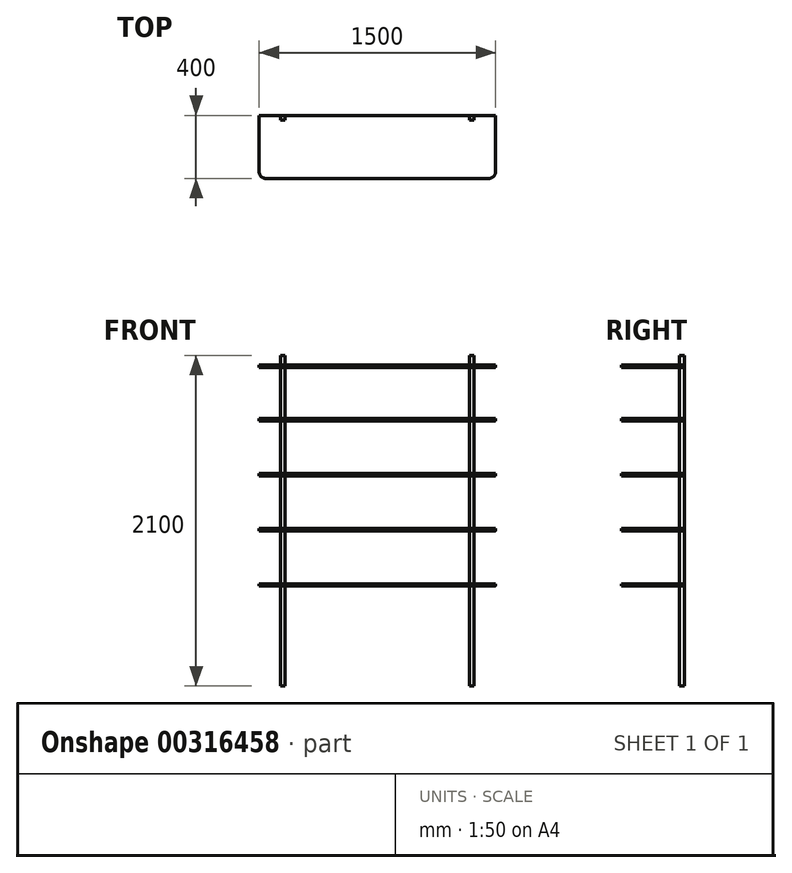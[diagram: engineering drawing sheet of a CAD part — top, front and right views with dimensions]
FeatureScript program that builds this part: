
annotation { "Feature Type Name" : "Feature", "Feature Type Description" : "" }
export const myFeature = defineFeature(function(context is Context, id is Id, definition is map)
    precondition{}
    {
        {
            assignVariable(context, id + "F0", {"name" : "Hauteur", "anyValue" : 2100});
        }
        {
            assignVariable(context, id + "F1", {"name" : "Ep", "anyValue" : 15});
        }
        {
            assignVariable(context, id + "F2", {"name" : "Niveau1", "anyValue" : 650});
        }
        {
            assignVariable(context, id + "F3", {"name" : "Niveau2", "anyValue" : 1000});
        }
        {
            assignVariable(context, id + "F4", {"name" : "Niveau3", "anyValue" : 1350});
        }
        {
            assignVariable(context, id + "F5", {"name" : "Niveau4", "anyValue" : 1700});
        }
        {
            assignVariable(context, id + "F6", {"name" : "Niveau5", "anyValue" : 2040});
        }
        {
            var Q0;
            Q0=qCreatedBy(makeId("Top.planeOp"),FACE);
            var sketch = newSketch(context, id + "F7", { "sketchPlane" : qUnion([Q0])});
            skLineSegment(sketch, "E0.bottom", {"start": v(-615, 0) * mm, "end": v(-585, 0) * mm});
            skLineSegment(sketch, "E0.top", {"start": v(-615, -30) * mm, "end": v(-585, -30) * mm});
            skLineSegment(sketch, "E0.left", {"start": v(-615, 0) * mm, "end": v(-615, -30) * mm});
            skLineSegment(sketch, "E0.right", {"start": v(-585, 0) * mm, "end": v(-585, -30) * mm});
            skLineSegment(sketch, "E1", {"start": v(0, 0) * mm, "end": v(0, -268.34) * mm, "construction": true});
            skLineSegment(sketch, "E2.MirrorCS", {"start": v(615, 0) * mm, "end": v(585, 0) * mm});
            skLineSegment(sketch, "E3.MirrorCS", {"start": v(615, -30) * mm, "end": v(585, -30) * mm});
            skLineSegment(sketch, "E4.MirrorCS", {"start": v(615, 0) * mm, "end": v(615, -30) * mm});
            skLineSegment(sketch, "E5.MirrorCS", {"start": v(585, 0) * mm, "end": v(585, -30) * mm});
            skSolve(sketch);
        }
        {
            var Q0;
            Q0=makeQuery(id+"F7.imprint","IMPRINT",FACE,{"disambiguationData":[TD([[makeQuery(id+"F7.imprint","IMPRINT",EDGE,{"derivedFrom":sQuery(id+"F7.wireOp",EDGE,"E0.bottom")}),-1.0]])]});
            var Q1;
            Q1=makeQuery(id+"F7.imprint","IMPRINT",FACE,{"disambiguationData":[TD([[makeQuery(id+"F7.imprint","IMPRINT",EDGE,{"derivedFrom":sQuery(id+"F7.wireOp",EDGE,"E2.MirrorCS")}),1.0]])]});
            extrude(context, id + "F8", {"entities" : qUnion([Q0, Q1]), "depth" : (getVariable(context, 'Hauteur')) * mm});
        }
        {
            var Q0;
            Q0=qCreatedBy(makeId("Top.planeOp"),FACE);
            cPlane(context, id + "F9", {"entities" : qUnion([Q0]), "cplaneType" : CPlaneType.OFFSET, "offset" : (getVariable(context, 'Niveau1')) * mm, "width" : 150 * mm, "height" : 150 * mm});
        }
        {
            var Q0;
            Q0=qCreatedBy(makeId("Top.planeOp"),FACE);
            cPlane(context, id + "F10", {"entities" : qUnion([Q0]), "cplaneType" : CPlaneType.OFFSET, "offset" : (getVariable(context, 'Niveau2')) * mm, "width" : 150 * mm, "height" : 150 * mm});
        }
        {
            var Q0;
            Q0=qCreatedBy(makeId("Top.planeOp"),FACE);
            cPlane(context, id + "F11", {"entities" : qUnion([Q0]), "cplaneType" : CPlaneType.OFFSET, "offset" : (getVariable(context, 'Niveau3')) * mm, "width" : 150 * mm, "height" : 150 * mm});
        }
        {
            var Q0;
            Q0=qCreatedBy(makeId("Top.planeOp"),FACE);
            cPlane(context, id + "F12", {"entities" : qUnion([Q0]), "cplaneType" : CPlaneType.OFFSET, "offset" : (getVariable(context, 'Niveau4')) * mm, "width" : 150 * mm, "height" : 150 * mm});
        }
        {
            var Q0;
            Q0=qCreatedBy(makeId("Top.planeOp"),FACE);
            cPlane(context, id + "F13", {"entities" : qUnion([Q0]), "cplaneType" : CPlaneType.OFFSET, "offset" : (getVariable(context, 'Niveau5')) * mm, "width" : 150 * mm, "height" : 150 * mm});
        }
        {
            var Q0;
            Q0=qCreatedBy(id+"F9.planeOp",FACE);
            var sketch = newSketch(context, id + "F14", { "sketchPlane" : qUnion([Q0])});
            skLineSegment(sketch, "E6", {"start": v(0, 0) * mm, "end": v(0, -284.12) * mm, "construction": true});
            skLineSegment(sketch, "E7", {"start": v(0, 0) * mm, "end": v(-585, 0) * mm});
            skLineSegment(sketch, "E8", {"start": v(-750, 0) * mm, "end": v(-750, -360) * mm});
            skLineSegment(sketch, "E9", {"start": v(-710, -400) * mm, "end": v(0, -400) * mm});
            skPoint(sketch, "E10.visualSharp", {"position": v(-750, -400) * mm});
            skArc(sketch, "E10.filletArc", {"start": v(-750, -360) * mm, "mid": v(-738.28, -388.28) * mm, "end": v(-710, -400) * mm});
            skLineSegment(sketch, "E11.0", {"start": v(-615, 0) * mm, "end": v(-615, -30) * mm});
            skLineSegment(sketch, "E12.0", {"start": v(-615, -30) * mm, "end": v(-585, -30) * mm});
            skLineSegment(sketch, "E13.0", {"start": v(-585, 0) * mm, "end": v(-585, -30) * mm});
            skLineSegment(sketch, "E14.trimOffspring", {"start": v(-615, 0) * mm, "end": v(-750, 0) * mm});
            skLineSegment(sketch, "E15.MirrorCS", {"start": v(0, 0) * mm, "end": v(585, 0) * mm});
            skLineSegment(sketch, "E16.MirrorCS", {"start": v(585, 0) * mm, "end": v(585, -30) * mm});
            skLineSegment(sketch, "E17.MirrorCS", {"start": v(615, -30) * mm, "end": v(585, -30) * mm});
            skLineSegment(sketch, "E18.MirrorCS", {"start": v(615, 0) * mm, "end": v(615, -30) * mm});
            skLineSegment(sketch, "E19.MirrorCS", {"start": v(615, 0) * mm, "end": v(750, 0) * mm});
            skLineSegment(sketch, "E20.MirrorCS", {"start": v(750, 0) * mm, "end": v(750, -360) * mm});
            skArc(sketch, "E21.MirrorCS", {"start": v(750, -360) * mm, "mid": v(738.28, -388.28) * mm, "end": v(710, -400) * mm});
            skLineSegment(sketch, "E22.MirrorCS", {"start": v(710, -400) * mm, "end": v(0, -400) * mm});
            skSolve(sketch);
        }
        {
            var Q0;
            Q0=makeQuery(id+"F14.imprint","IMPRINT",FACE,{"disambiguationData":[TD([[makeQuery(id+"F14.imprint","IMPRINT",EDGE,{"derivedFrom":sQuery(id+"F14.wireOp",EDGE,"E7")}),1.0]])]});
            extrude(context, id + "F15", {"entities" : qUnion([Q0]), "oppositeDirection" : true, "depth" : (getVariable(context, 'Ep')) * mm});
        }
        {
            var Q0;
            Q0=qCreatedBy(id+"F10.planeOp",FACE);
            var sketch = newSketch(context, id + "F16", { "sketchPlane" : qUnion([Q0])});
            skLineSegment(sketch, "E23.0", {"start": v(710, -400) * mm, "end": v(0, -400) * mm});
            skLineSegment(sketch, "E23.1", {"start": v(615, 0) * mm, "end": v(750, 0) * mm});
            skLineSegment(sketch, "E23.2", {"start": v(750, 0) * mm, "end": v(750, -360) * mm});
            skLineSegment(sketch, "E23.4", {"start": v(0, 0) * mm, "end": v(-585, 0) * mm});
            skLineSegment(sketch, "E23.5", {"start": v(-750, 0) * mm, "end": v(-750, -360) * mm});
            skLineSegment(sketch, "E23.6", {"start": v(-710, -400) * mm, "end": v(0, -400) * mm});
            skLineSegment(sketch, "E23.7", {"start": v(-615, 0) * mm, "end": v(-750, 0) * mm});
            skLineSegment(sketch, "E23.8", {"start": v(0, 0) * mm, "end": v(585, 0) * mm});
            skLineSegment(sketch, "E23.9", {"start": v(750, 0) * mm, "end": v(750, -360) * mm});
            skArc(sketch, "E24.0", {"start": v(-750, -360) * mm, "mid": v(-738.28, -388.28) * mm, "end": v(-710, -400) * mm});
            skArc(sketch, "E25.0", {"start": v(750, -360) * mm, "mid": v(738.28, -388.28) * mm, "end": v(710, -400) * mm});
            skLineSegment(sketch, "E26.0", {"start": v(-615, -30) * mm, "end": v(-585, -30) * mm});
            skLineSegment(sketch, "E27.0", {"start": v(-615, 0) * mm, "end": v(-615, -30) * mm});
            skLineSegment(sketch, "E28.0", {"start": v(-585, 0) * mm, "end": v(-585, -30) * mm});
            skLineSegment(sketch, "E29.0", {"start": v(585, 0) * mm, "end": v(585, -30) * mm});
            skLineSegment(sketch, "E30.0", {"start": v(615, -30) * mm, "end": v(585, -30) * mm});
            skPoint(sketch, "E31.0", {"position": v(615, -15) * mm});
            skLineSegment(sketch, "E32.0", {"start": v(615, 0) * mm, "end": v(615, -30) * mm});
            skSolve(sketch);
        }
        {
            var Q0;
            Q0=makeQuery(id+"F16.imprint","IMPRINT",FACE,{"disambiguationData":[TD([[makeQuery(id+"F16.imprint","IMPRINT",EDGE,{"derivedFrom":sQuery(id+"F16.wireOp",EDGE,"E23.0")}),-1.0]])]});
            extrude(context, id + "F17", {"entities" : qUnion([Q0]), "oppositeDirection" : true, "depth" : (getVariable(context, 'Ep')) * mm});
        }
        {
            var Q0;
            Q0=qCreatedBy(id+"F11.planeOp",FACE);
            var sketch = newSketch(context, id + "F18", { "sketchPlane" : qUnion([Q0])});
            skLineSegment(sketch, "E33.0", {"start": v(710, -400) * mm, "end": v(0, -400) * mm});
            skLineSegment(sketch, "E33.1", {"start": v(615, 0) * mm, "end": v(750, 0) * mm});
            skLineSegment(sketch, "E33.2", {"start": v(750, 0) * mm, "end": v(750, -360) * mm});
            skLineSegment(sketch, "E33.4", {"start": v(0, 0) * mm, "end": v(-585, 0) * mm});
            skLineSegment(sketch, "E33.5", {"start": v(-750, 0) * mm, "end": v(-750, -360) * mm});
            skLineSegment(sketch, "E33.6", {"start": v(-710, -400) * mm, "end": v(0, -400) * mm});
            skLineSegment(sketch, "E33.7", {"start": v(-615, 0) * mm, "end": v(-750, 0) * mm});
            skLineSegment(sketch, "E33.8", {"start": v(0, 0) * mm, "end": v(585, 0) * mm});
            skLineSegment(sketch, "E33.9", {"start": v(750, 0) * mm, "end": v(750, -360) * mm});
            skLineSegment(sketch, "E33.10", {"start": v(-710, -400) * mm, "end": v(710, -400) * mm});
            skArc(sketch, "E34.0", {"start": v(-750, -360) * mm, "mid": v(-738.28, -388.28) * mm, "end": v(-710, -400) * mm});
            skLineSegment(sketch, "E35.0", {"start": v(-615, 0) * mm, "end": v(-615, -30) * mm});
            skLineSegment(sketch, "E36.0", {"start": v(-615, -30) * mm, "end": v(-585, -30) * mm});
            skLineSegment(sketch, "E37.0", {"start": v(-585, 0) * mm, "end": v(-585, -30) * mm});
            skLineSegment(sketch, "E38.0", {"start": v(585, 0) * mm, "end": v(585, -30) * mm});
            skLineSegment(sketch, "E39.0", {"start": v(615, -30) * mm, "end": v(585, -30) * mm});
            skLineSegment(sketch, "E40.0", {"start": v(615, 0) * mm, "end": v(615, -30) * mm});
            skArc(sketch, "E41.0", {"start": v(750, -360) * mm, "mid": v(738.28, -388.28) * mm, "end": v(710, -400) * mm});
            skSolve(sketch);
        }
        {
            var Q0;
            Q0=makeQuery(id+"F18.imprint","IMPRINT",FACE,{"disambiguationData":[TD([[makeQuery(id+"F18.imprint","IMPRINT",EDGE,{"derivedFrom":sQuery(id+"F18.wireOp",EDGE,"E33.1")}),-1.0]])]});
            extrude(context, id + "F19", {"entities" : qUnion([Q0]), "oppositeDirection" : true, "depth" : (getVariable(context, 'Ep')) * mm});
        }
        {
            var Q0;
            Q0=qCreatedBy(id+"F12.planeOp",FACE);
            var sketch = newSketch(context, id + "F20", { "sketchPlane" : qUnion([Q0])});
            skPoint(sketch, "E42.0", {"position": v(710, -400) * mm});
            skLineSegment(sketch, "E43.0", {"start": v(710, -400) * mm, "end": v(0, -400) * mm});
            skLineSegment(sketch, "E43.1", {"start": v(615, 0) * mm, "end": v(750, 0) * mm});
            skLineSegment(sketch, "E43.2", {"start": v(750, 0) * mm, "end": v(750, -360) * mm});
            skArc(sketch, "E43.3", {"start": v(750, -360) * mm, "mid": v(738.28, -388.28) * mm, "end": v(710, -400) * mm});
            skLineSegment(sketch, "E43.5", {"start": v(0, 0) * mm, "end": v(-585, 0) * mm});
            skLineSegment(sketch, "E43.6", {"start": v(-750, 0) * mm, "end": v(-750, -360) * mm});
            skLineSegment(sketch, "E43.7", {"start": v(-710, -400) * mm, "end": v(0, -400) * mm});
            skLineSegment(sketch, "E43.8", {"start": v(-615, 0) * mm, "end": v(-750, 0) * mm});
            skLineSegment(sketch, "E43.9", {"start": v(0, 0) * mm, "end": v(585, 0) * mm});
            skLineSegment(sketch, "E43.10", {"start": v(750, 0) * mm, "end": v(750, -360) * mm});
            skLineSegment(sketch, "E43.11", {"start": v(-710, -400) * mm, "end": v(710, -400) * mm});
            skArc(sketch, "E43.12", {"start": v(750, -360) * mm, "mid": v(738.28, -388.28) * mm, "end": v(710, -400) * mm});
            skLineSegment(sketch, "E44.0", {"start": v(615, 0) * mm, "end": v(615, -30) * mm});
            skLineSegment(sketch, "E45.0", {"start": v(615, -30) * mm, "end": v(585, -30) * mm});
            skLineSegment(sketch, "E46.0", {"start": v(585, 0) * mm, "end": v(585, -30) * mm});
            skLineSegment(sketch, "E47.0", {"start": v(-615, 0) * mm, "end": v(-615, -30) * mm});
            skLineSegment(sketch, "E48.0", {"start": v(-615, -30) * mm, "end": v(-585, -30) * mm});
            skLineSegment(sketch, "E49.0", {"start": v(-585, 0) * mm, "end": v(-585, -30) * mm});
            skPoint(sketch, "E50.0", {"position": v(-738.28, -388.28) * mm});
            skArc(sketch, "E51.0", {"start": v(-750, -360) * mm, "mid": v(-738.28, -388.28) * mm, "end": v(-710, -400) * mm});
            skSolve(sketch);
        }
        {
            var Q0;
            Q0=makeQuery(id+"F20.imprint","IMPRINT",FACE,{"disambiguationData":[TD([[makeQuery(id+"F20.imprint","IMPRINT",EDGE,{"derivedFrom":sQuery(id+"F20.wireOp",EDGE,"E43.1")}),-1.0]])]});
            extrude(context, id + "F21", {"entities" : qUnion([Q0]), "oppositeDirection" : true, "depth" : (getVariable(context, 'Ep')) * mm});
        }
        {
            var Q0;
            Q0=qCreatedBy(id+"F13.planeOp",FACE);
            var sketch = newSketch(context, id + "F22", { "sketchPlane" : qUnion([Q0])});
            skLineSegment(sketch, "E52.0", {"start": v(710, -400) * mm, "end": v(0, -400) * mm});
            skLineSegment(sketch, "E52.1", {"start": v(615, 0) * mm, "end": v(750, 0) * mm});
            skLineSegment(sketch, "E52.2", {"start": v(750, 0) * mm, "end": v(750, -360) * mm});
            skLineSegment(sketch, "E52.4", {"start": v(0, 0) * mm, "end": v(-585, 0) * mm});
            skLineSegment(sketch, "E52.5", {"start": v(-750, 0) * mm, "end": v(-750, -360) * mm});
            skLineSegment(sketch, "E52.6", {"start": v(-710, -400) * mm, "end": v(0, -400) * mm});
            skLineSegment(sketch, "E52.7", {"start": v(-615, 0) * mm, "end": v(-750, 0) * mm});
            skLineSegment(sketch, "E52.8", {"start": v(0, 0) * mm, "end": v(585, 0) * mm});
            skLineSegment(sketch, "E52.9", {"start": v(-710, -400) * mm, "end": v(710, -400) * mm});
            skLineSegment(sketch, "E52.10", {"start": v(-710, -400) * mm, "end": v(710, -400) * mm});
            skLineSegment(sketch, "E52.11", {"start": v(750, 0) * mm, "end": v(750, -360) * mm});
            skLineSegment(sketch, "E52.12", {"start": v(-750, 0) * mm, "end": v(-750, -360) * mm});
            skLineSegment(sketch, "E52.13", {"start": v(750, 0) * mm, "end": v(750, -360) * mm});
            skLineSegment(sketch, "E52.14", {"start": v(-585, 0) * mm, "end": v(585, 0) * mm});
            skLineSegment(sketch, "E52.15", {"start": v(750, 0) * mm, "end": v(750, -360) * mm});
            skLineSegment(sketch, "E52.16", {"start": v(-710, -400) * mm, "end": v(710, -400) * mm});
            skArc(sketch, "E53.0", {"start": v(750, -360) * mm, "mid": v(738.28, -388.28) * mm, "end": v(710, -400) * mm});
            skLineSegment(sketch, "E54.0", {"start": v(615, 0) * mm, "end": v(615, -30) * mm});
            skLineSegment(sketch, "E55.0", {"start": v(615, -30) * mm, "end": v(585, -30) * mm});
            skLineSegment(sketch, "E56.0", {"start": v(585, 0) * mm, "end": v(585, -30) * mm});
            skLineSegment(sketch, "E57.0", {"start": v(-585, 0) * mm, "end": v(-585, -30) * mm});
            skLineSegment(sketch, "E58.0", {"start": v(-615, -30) * mm, "end": v(-585, -30) * mm});
            skLineSegment(sketch, "E59.0", {"start": v(-615, 0) * mm, "end": v(-615, -30) * mm});
            skArc(sketch, "E60.0", {"start": v(-750, -360) * mm, "mid": v(-738.28, -388.28) * mm, "end": v(-710, -400) * mm});
            skSolve(sketch);
        }
        {
            var Q0;
            Q0=makeQuery(id+"F22.imprint","IMPRINT",FACE,{"disambiguationData":[TD([[makeQuery(id+"F22.imprint","IMPRINT",EDGE,{"derivedFrom":sQuery(id+"F22.wireOp",EDGE,"E52.1")}),-1.0]])]});
            extrude(context, id + "F23", {"entities" : qUnion([Q0]), "oppositeDirection" : true, "depth" : (getVariable(context, 'Ep')) * mm});
        }
    });
